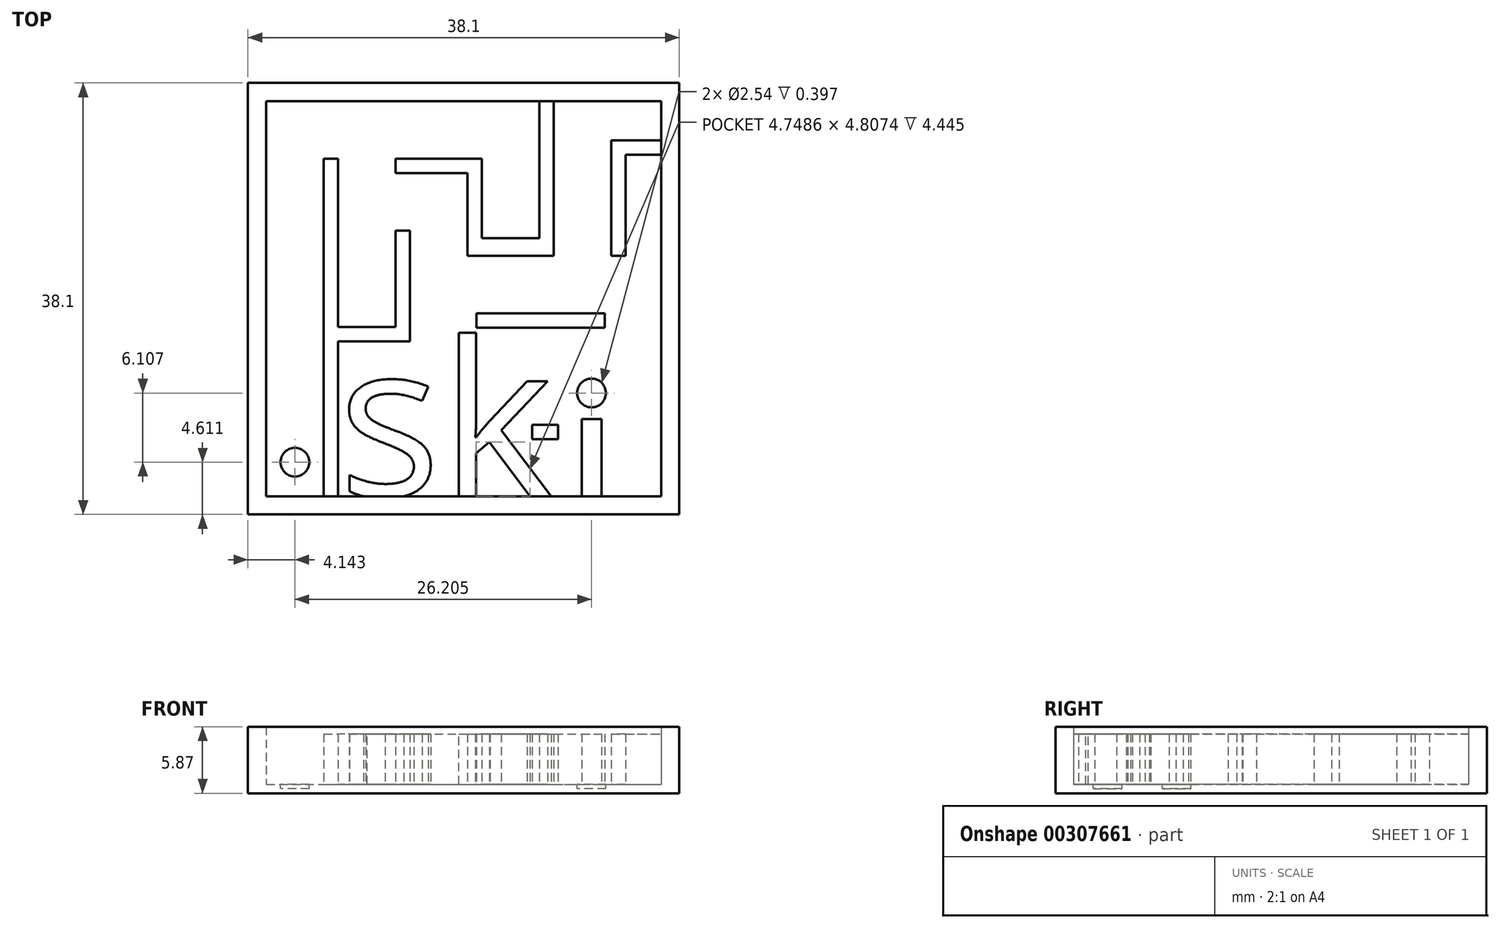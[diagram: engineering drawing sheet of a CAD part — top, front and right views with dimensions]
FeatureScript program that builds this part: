
annotation { "Feature Type Name" : "Feature", "Feature Type Description" : "" }
export const myFeature = defineFeature(function(context is Context, id is Id, definition is map)
    precondition{}
    {
        {
            var Q0;
            Q0=qCreatedBy(makeId("Top.planeOp"),FACE);
            var sketch = newSketch(context, id + "F0", { "sketchPlane" : qUnion([Q0])});
            skLineSegment(sketch, "E0.bottom", {"start": v(-18.63, 17.52) * mm, "end": v(19.47, 17.52) * mm});
            skLineSegment(sketch, "E0.top", {"start": v(-18.63, -20.58) * mm, "end": v(19.47, -20.58) * mm});
            skLineSegment(sketch, "E0.left", {"start": v(-18.63, 17.52) * mm, "end": v(-18.63, -20.58) * mm});
            skLineSegment(sketch, "E0.right", {"start": v(19.47, 17.52) * mm, "end": v(19.47, -20.58) * mm});
            skSolve(sketch);
        }
        {
            var Q0;
            Q0 = qSketchRegion(id + "F0", true);
            extrude(context, id + "F1", {"entities" : qUnion([Q0]), "depth" : 0.8 * mm});
        }
        {
            var Q0;
            Q0=makeQuery(id+"F1.opExtrude","CAP_FACE",FACE,{"disambiguationData":[OSD([sQuery(id+"F0.wireOp",EDGE,"E0.bottom"),sQuery(id+"F0.wireOp",EDGE,"E0.top"),sQuery(id+"F0.wireOp",EDGE,"E0.left"),sQuery(id+"F0.wireOp",EDGE,"E0.right")])],"isStart":false});
            var sketch = newSketch(context, id + "F2", { "sketchPlane" : qUnion([Q0])});
            skLineSegment(sketch, "E1.0", {"start": v(-17.03, 15.92) * mm, "end": v(17.87, 15.92) * mm});
            skLineSegment(sketch, "E1.1", {"start": v(-17.03, 15.92) * mm, "end": v(-17.03, -18.98) * mm});
            skLineSegment(sketch, "E1.2", {"start": v(-17.03, -18.98) * mm, "end": v(17.87, -18.98) * mm});
            skLineSegment(sketch, "E1.3", {"start": v(17.87, 15.92) * mm, "end": v(17.87, -18.98) * mm});
            skSolve(sketch);
        }
        {
            var Q0;
            Q0=makeQuery(id+"F2.imprint","IMPRINT",FACE,{"disambiguationData":[TD([[makeQuery(id+"F2.imprint","IMPRINT",EDGE,{"derivedFrom":sQuery(id+"F2.wireOp",EDGE,"E1.0")}),1.0]])]});
            extrude(context, id + "F3", {"entities" : qUnion([Q0]), "operationType" : NewBodyOperationType.ADD, "depth" : 5.08 * mm});
        }
        {
            var Q0;
            Q0=makeQuery(id+"F1.opExtrude","CAP_FACE",FACE,{"disambiguationData":[OSD([sQuery(id+"F0.wireOp",EDGE,"E0.bottom"),sQuery(id+"F0.wireOp",EDGE,"E0.top"),sQuery(id+"F0.wireOp",EDGE,"E0.left"),sQuery(id+"F0.wireOp",EDGE,"E0.right")])],"isStart":false});
            var sketch = newSketch(context, id + "F4", { "sketchPlane" : qUnion([Q0])});
            skLineSegment(sketch, "E2.bottom", {"start": v(-11.95, -18.98) * mm, "end": v(-10.68, -18.98) * mm});
            skLineSegment(sketch, "E2.top", {"start": v(-11.95, 10.84) * mm, "end": v(-10.68, 10.84) * mm});
            skLineSegment(sketch, "E2.left", {"start": v(-11.95, -18.98) * mm, "end": v(-11.95, 10.84) * mm});
            skLineSegment(sketch, "E2.right", {"start": v(-10.68, -18.98) * mm, "end": v(-10.68, -5.31) * mm});
            skLineSegment(sketch, "E3", {"start": v(-5.6, 10.84) * mm, "end": v(2.02, 10.84) * mm});
            skLineSegment(sketch, "E4.bottom", {"start": v(7.1, 15.92) * mm, "end": v(8.37, 15.92) * mm});
            skLineSegment(sketch, "E5", {"start": v(-5.6, 10.84) * mm, "end": v(-5.6, 9.57) * mm});
            skLineSegment(sketch, "E6", {"start": v(-5.6, 9.57) * mm, "end": v(0.75, 9.57) * mm});
            skLineSegment(sketch, "E7", {"start": v(0.75, 7.45) * mm, "end": v(2.02, 7.45) * mm});
            skLineSegment(sketch, "E8", {"start": v(2.02, 8.72) * mm, "end": v(2.02, 8.72) * mm});
            skPoint(sketch, "E9.orphan", {"position": v(2.02, 9.57) * mm});
            skLineSegment(sketch, "E10", {"start": v(2.02, 7.45) * mm, "end": v(2.02, 7.45) * mm});
            skLineSegment(sketch, "E11", {"start": v(7.1, 3.82) * mm, "end": v(1.86, 3.82) * mm});
            skLineSegment(sketch, "E12", {"start": v(2.02, 7.45) * mm, "end": v(2.02, 3.82) * mm});
            skLineSegment(sketch, "E13", {"start": v(0.75, 7.45) * mm, "end": v(0.75, 2.25) * mm});
            skLineSegment(sketch, "E14", {"start": v(0.75, 9.57) * mm, "end": v(0.75, 7.45) * mm});
            skLineSegment(sketch, "E15.bottom", {"start": v(-5.6, 4.49) * mm, "end": v(-4.33, 4.49) * mm});
            skLineSegment(sketch, "E15.left", {"start": v(-5.6, 4.49) * mm, "end": v(-5.6, -4.04) * mm});
            skLineSegment(sketch, "E15.right", {"start": v(-4.33, 4.49) * mm, "end": v(-4.33, -4.04) * mm});
            skLineSegment(sketch, "E16.bottom", {"start": v(-5.6, -4.04) * mm, "end": v(-10.68, -4.04) * mm});
            skLineSegment(sketch, "E16.top", {"start": v(-4.33, -5.31) * mm, "end": v(-10.68, -5.31) * mm});
            skLineSegment(sketch, "E16.left", {"start": v(-4.33, -4.04) * mm, "end": v(-4.33, -5.31) * mm});
            skLineSegment(sketch, "E17.trimOffspring", {"start": v(-10.68, -4.04) * mm, "end": v(-10.68, 10.84) * mm});
            skPoint(sketch, "E18.start.orphan", {"position": v(8.37, 10.84) * mm});
            skPoint(sketch, "E19.start.orphan", {"position": v(8.37, 7.45) * mm});
            skLineSegment(sketch, "E20", {"start": v(8.37, 15.92) * mm, "end": v(8.37, 2.25) * mm});
            skLineSegment(sketch, "E21", {"start": v(7.1, 3.82) * mm, "end": v(7.1, 15.92) * mm});
            skPoint(sketch, "E22.end.orphan", {"position": v(1.86, 2.25) * mm});
            skLineSegment(sketch, "E23", {"start": v(0.75, 2.25) * mm, "end": v(8.37, 2.25) * mm});
            skLineSegment(sketch, "E24", {"start": v(2.02, 10.84) * mm, "end": v(2.02, 7.45) * mm});
            skLineSegment(sketch, "E25", {"start": v(1.55, -2.83) * mm, "end": v(12.9, -2.83) * mm});
            skLineSegment(sketch, "E26", {"start": v(1.55, -2.83) * mm, "end": v(1.55, -4.1) * mm});
            skLineSegment(sketch, "E27", {"start": v(1.55, -4.1) * mm, "end": v(12.9, -4.1) * mm});
            skLineSegment(sketch, "E28", {"start": v(12.9, -4.1) * mm, "end": v(12.9, -2.83) * mm});
            skLineSegment(sketch, "E29.bottom", {"start": v(14.72, 2.25) * mm, "end": v(13.45, 2.25) * mm});
            skLineSegment(sketch, "E29.left", {"start": v(14.72, 2.25) * mm, "end": v(14.72, 11.17) * mm});
            skLineSegment(sketch, "E30.top", {"start": v(14.72, 11.17) * mm, "end": v(17.87, 11.17) * mm});
            skLineSegment(sketch, "E30.right", {"start": v(17.87, 12.44) * mm, "end": v(17.87, 11.17) * mm});
            skLineSegment(sketch, "E31", {"start": v(13.45, 2.25) * mm, "end": v(13.45, 12.44) * mm});
            skLineSegment(sketch, "E32", {"start": v(13.45, 12.44) * mm, "end": v(17.87, 12.44) * mm});
            skLineSegment(sketch, "E33.bottom", {"start": v(6.49, -12.67) * mm, "end": v(8.77, -12.67) * mm});
            skLineSegment(sketch, "E33.top", {"start": v(6.49, -13.94) * mm, "end": v(8.77, -13.94) * mm});
            skLineSegment(sketch, "E33.left", {"start": v(6.49, -12.67) * mm, "end": v(6.49, -13.94) * mm});
            skLineSegment(sketch, "E33.right", {"start": v(8.77, -12.67) * mm, "end": v(8.77, -13.94) * mm});
            skText(sketch, "E34", { "text": "sk", "fontName": "OpenSans-Regular.ttf"});
            skPoint(sketch, "E35.firstSnap0", {"position": v(9.38, -12.15) * mm});
            skLineSegment(sketch, "E35.bottom", {"start": v(10.84, -12.15) * mm, "end": v(12.6, -12.15) * mm});
            skLineSegment(sketch, "E35.top", {"start": v(10.84, -18.98) * mm, "end": v(12.6, -18.98) * mm});
            skLineSegment(sketch, "E35.left", {"start": v(10.84, -12.15) * mm, "end": v(10.84, -18.98) * mm});
            skLineSegment(sketch, "E35.right", {"start": v(12.6, -12.15) * mm, "end": v(12.6, -18.98) * mm});
            skPoint(sketch, "E36.centerSnap0", {"position": v(11.72, -12.15) * mm});
            const initialGuessF4  = {"E34": [-0.01068, -0.01898, 1, 0, 0.01367]};
            skSetInitialGuess(sketch, initialGuessF4);
            skSolve(sketch);
        }
        {
            var Q0;
            Q0 = qSketchRegion(id + "F4", true);
            extrude(context, id + "F5", {"entities" : qUnion([Q0]), "operationType" : NewBodyOperationType.ADD, "depth" : 4.44 * mm});
        }
        {
            var Q0;
            Q0=makeQuery(id+"F5.boolean.opBoolean","SPLIT",FACE,{"disambiguationData":[TD([makeQuery(id+"F3.opExtrude","SWEPT_FACE",FACE,{"disambiguationData":[OSD([sQuery(id+"F2.wireOp",EDGE,"E1.0")])]})])],"derivedFrom":makeQuery(id+"F1.opExtrude","CAP_FACE",FACE,{"disambiguationData":[OSD([sQuery(id+"F0.wireOp",EDGE,"E0.bottom"),sQuery(id+"F0.wireOp",EDGE,"E0.top"),sQuery(id+"F0.wireOp",EDGE,"E0.left"),sQuery(id+"F0.wireOp",EDGE,"E0.right")])],"isStart":false})});
            var sketch = newSketch(context, id + "F6", { "sketchPlane" : qUnion([Q0])});
            skCircle(sketch, "E37", {"center": v(11.72, -9.86) * mm, "radius": 1.27 * mm});
            skPoint(sketch, "E37.centerSnap0", {"position": v(11.72, -12.15) * mm});
            skSolve(sketch);
        }
        {
            var Q0;
            Q0=makeQuery(id+"F6.imprint","IMPRINT",FACE,{"disambiguationData":[TD([[makeQuery(id+"F6.imprint","IMPRINT",EDGE,{"derivedFrom":sQuery(id+"F6.wireOp",EDGE,"E37")}),1.0]])]});
            extrude(context, id + "F7", {"entities" : qUnion([Q0]), "operationType" : NewBodyOperationType.REMOVE, "oppositeDirection" : true, "depth" : 0.4 * mm});
        }
        {
            var Q0;
            Q0=makeQuery(id+"F5.boolean.opBoolean","SPLIT",FACE,{"disambiguationData":[TD([makeQuery(id+"F3.opExtrude","SWEPT_FACE",FACE,{"disambiguationData":[OSD([sQuery(id+"F2.wireOp",EDGE,"E1.0")])]})])],"derivedFrom":makeQuery(id+"F1.opExtrude","CAP_FACE",FACE,{"disambiguationData":[OSD([sQuery(id+"F0.wireOp",EDGE,"E0.bottom"),sQuery(id+"F0.wireOp",EDGE,"E0.top"),sQuery(id+"F0.wireOp",EDGE,"E0.left"),sQuery(id+"F0.wireOp",EDGE,"E0.right")])],"isStart":false})});
            var sketch = newSketch(context, id + "F8", { "sketchPlane" : qUnion([Q0])});
            skCircle(sketch, "E38", {"center": v(-14.49, -15.97) * mm, "radius": 1.27 * mm});
            skPoint(sketch, "E38.centerSnap0", {"position": v(-14.49, -18.98) * mm});
            skSolve(sketch);
        }
        {
            var Q0;
            Q0 = qSketchRegion(id + "F8", true);
            extrude(context, id + "F9", {"entities" : qUnion([Q0]), "operationType" : NewBodyOperationType.REMOVE, "oppositeDirection" : true, "depth" : 0.4 * mm});
        }
    });
